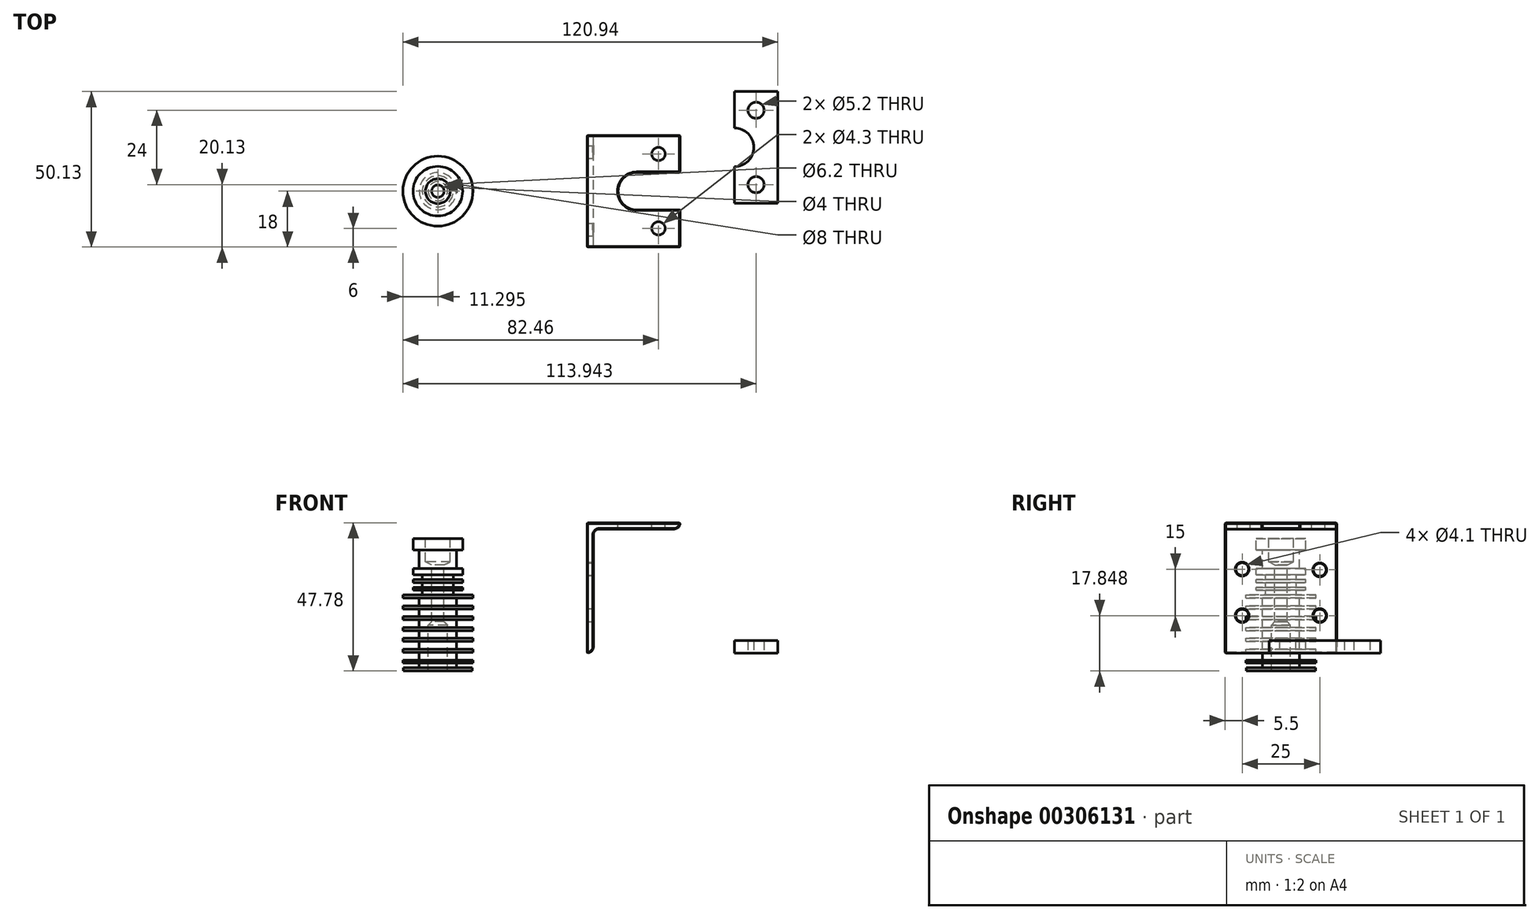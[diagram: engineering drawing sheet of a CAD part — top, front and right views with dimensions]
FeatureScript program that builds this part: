
annotation { "Feature Type Name" : "Feature", "Feature Type Description" : "" }
export const myFeature = defineFeature(function(context is Context, id is Id, definition is map)
    precondition{}
    {
        {
            var Q0;
            Q0=qCreatedBy(makeId("Front.planeOp"),FACE);
            var sketch = newSketch(context, id + "F0", { "sketchPlane" : qUnion([Q0])});
            skLineSegment(sketch, "E0", {"start": v(0, 0) * mm, "end": v(0, 42) * mm});
            skLineSegment(sketch, "E1", {"start": v(0, 42) * mm, "end": v(30, 42) * mm});
            skLineSegment(sketch, "E2", {"start": v(30, 42) * mm, "end": v(30, 40) * mm});
            skLineSegment(sketch, "E3", {"start": v(30, 40) * mm, "end": v(2, 40) * mm});
            skLineSegment(sketch, "E4", {"start": v(2, 40) * mm, "end": v(2, 0) * mm});
            skLineSegment(sketch, "E5", {"start": v(2, 0) * mm, "end": v(0, 0) * mm});
            skSolve(sketch);
        }
        {
            var Q0;
            Q0=makeQuery(id+"F0.imprint","IMPRINT",FACE,{"disambiguationData":[TD([[makeQuery(id+"F0.imprint","IMPRINT",EDGE,{"derivedFrom":sQuery(id+"F0.wireOp",EDGE,"E0")}),-1.0]])]});
            extrude(context, id + "F1", {"entities" : qUnion([Q0]), "endBound" : BoundingType.SYMMETRIC, "depth" : 36 * mm});
        }
        {
            var Q0;
            Q0=makeQuery(id+"F1.opExtrude","SWEPT_EDGE",EDGE,{"disambiguationData":[OSD([sQuery(id+"F0.wireOp",EDGE,"E3"),sQuery(id+"F0.wireOp",EDGE,"E4")])]});
            var Q1;
            Q1=makeQuery(id+"F1.opExtrude","SWEPT_EDGE",EDGE,{"disambiguationData":[OSD([sQuery(id+"F0.wireOp",EDGE,"E2"),sQuery(id+"F0.wireOp",EDGE,"E3")])]});
            var Q2;
            Q2=makeQuery(id+"F1.opExtrude","SWEPT_EDGE",EDGE,{"disambiguationData":[OSD([sQuery(id+"F0.wireOp",EDGE,"E4"),sQuery(id+"F0.wireOp",EDGE,"E5")])]});
            fillet(context, id + "F2", {"entities" : qUnion([Q0, Q1, Q2]), "radius" : 2 * mm, "tangentPropagation" : true, "allowEdgeOverflow" : false});
        }
        {
            var Q0;
            Q0=makeQuery(id+"F1.opExtrude","SWEPT_FACE",FACE,{"disambiguationData":[OSD([sQuery(id+"F0.wireOp",EDGE,"E1")])]});
            var sketch = newSketch(context, id + "F3", { "sketchPlane" : qUnion([Q0])});
            skArc(sketch, "E6", {"start": v(16, 6.03) * mm, "mid": v(9.97, 0) * mm, "end": v(16, -6.03) * mm});
            skLineSegment(sketch, "E7", {"start": v(16, -6.03) * mm, "end": v(30, -6.03) * mm});
            skLineSegment(sketch, "E8", {"start": v(16, 6.03) * mm, "end": v(30, 6.03) * mm});
            skLineSegment(sketch, "E9", {"start": v(30, -6.03) * mm, "end": v(30, 6.03) * mm});
            skCircle(sketch, "E10", {"center": v(23, 12) * mm, "radius": 2.15 * mm});
            skCircle(sketch, "E11", {"center": v(23, -12) * mm, "radius": 2.15 * mm});
            skSolve(sketch);
        }
        {
            var Q0;
            Q0=makeQuery(id+"F3.imprint","IMPRINT",FACE,{"disambiguationData":[TD([[makeQuery(id+"F3.imprint","IMPRINT",EDGE,{"derivedFrom":sQuery(id+"F3.wireOp",EDGE,"E6")}),1.0]])]});
            extrude(context, id + "F4", {"entities" : qUnion([Q0]), "operationType" : NewBodyOperationType.REMOVE, "oppositeDirection" : true, "depth" : 25 * mm});
        }
        {
            var Q0;
            Q0=makeQuery(id+"F1.opExtrude","SWEPT_FACE",FACE,{"disambiguationData":[OSD([sQuery(id+"F0.wireOp",EDGE,"E0")])]});
            var sketch = newSketch(context, id + "F5", { "sketchPlane" : qUnion([Q0])});
            skPoint(sketch, "E12", {"position": v(-12.5, 26.84) * mm});
            skPoint(sketch, "E13", {"position": v(-12.5, 12.07) * mm});
            skPoint(sketch, "E14", {"position": v(12.5, 12.07) * mm});
            skPoint(sketch, "E15", {"position": v(12.5, 27.07) * mm});
            skCircle(sketch, "E16", {"center": v(-12.5, 26.84) * mm, "radius": 2.05 * mm});
            skCircle(sketch, "E17", {"center": v(-12.5, 12.07) * mm, "radius": 2.05 * mm});
            skCircle(sketch, "E18", {"center": v(12.5, 12.07) * mm, "radius": 2.05 * mm});
            skCircle(sketch, "E19", {"center": v(12.5, 27.07) * mm, "radius": 2.05 * mm});
            skSolve(sketch);
        }
        {
            var Q0;
            Q0=makeQuery(id+"F5.imprint","IMPRINT",FACE,{"disambiguationData":[TD([[makeQuery(id+"F5.imprint","IMPRINT",EDGE,{"derivedFrom":sQuery(id+"F5.wireOp",EDGE,"E16")}),1.0]])]});
            var Q1;
            Q1=makeQuery(id+"F5.imprint","IMPRINT",FACE,{"disambiguationData":[TD([[makeQuery(id+"F5.imprint","IMPRINT",EDGE,{"derivedFrom":sQuery(id+"F5.wireOp",EDGE,"E17")}),1.0]])]});
            var Q2;
            Q2=makeQuery(id+"F5.imprint","IMPRINT",FACE,{"disambiguationData":[TD([[makeQuery(id+"F5.imprint","IMPRINT",EDGE,{"derivedFrom":sQuery(id+"F5.wireOp",EDGE,"E18")}),1.0]])]});
            var Q3;
            Q3=makeQuery(id+"F5.imprint","IMPRINT",FACE,{"disambiguationData":[TD([[makeQuery(id+"F5.imprint","IMPRINT",EDGE,{"derivedFrom":sQuery(id+"F5.wireOp",EDGE,"E19")}),1.0]])]});
            extrude(context, id + "F6", {"entities" : qUnion([Q0, Q1, Q2, Q3]), "operationType" : NewBodyOperationType.REMOVE, "oppositeDirection" : true, "depth" : 25 * mm});
        }
        {
            var Q0;
            Q0=makeQuery(id+"F1.opExtrude","SWEPT_FACE",FACE,{"disambiguationData":[OSD([sQuery(id+"F0.wireOp",EDGE,"E0")])]});
            var Q1;
            Q1=makeQuery(id+"F1.opExtrude","SWEPT_FACE",FACE,{"disambiguationData":[OSD([sQuery(id+"F0.wireOp",EDGE,"E1")])]});
            var Q2;
            Q2=makeQuery(id+"F1.opExtrude","SWEPT_FACE",FACE,{"disambiguationData":[OSD([sQuery(id+"F0.wireOp",EDGE,"E4")])]});
            var Q3;
            Q3=makeQuery(id+"F1.opExtrude","SWEPT_FACE",FACE,{"disambiguationData":[OSD([sQuery(id+"F0.wireOp",EDGE,"E3")])]});
            chamfer(context, id + "F7", {"entities" : qUnion([Q0, Q1, Q2, Q3]), "width" : 0.2 * mm, "tangentPropagation" : true});
        }
        {
            var Q0;
            Q0 = qSketchRegion(id + "F3", true);
            extrude(context, id + "F8", {"entities" : qUnion([Q0]), "operationType" : NewBodyOperationType.REMOVE, "oppositeDirection" : true, "depth" : 25 * mm});
        }
        {
            var Q0;
            Q0=qCreatedBy(makeId("Top.planeOp"),FACE);
            var sketch = newSketch(context, id + "F9", { "sketchPlane" : qUnion([Q0])});
            skLineSegment(sketch, "E20.bottom", {"start": v(47.48, -3.87) * mm, "end": v(61.48, -3.87) * mm});
            skLineSegment(sketch, "E20.top", {"start": v(47.48, 32.13) * mm, "end": v(61.48, 32.13) * mm});
            skLineSegment(sketch, "E20.left", {"start": v(47.48, -3.87) * mm, "end": v(47.48, 7.88) * mm});
            skLineSegment(sketch, "E20.right", {"start": v(61.48, -3.87) * mm, "end": v(61.48, 32.13) * mm});
            skArc(sketch, "E21", {"start": v(47.48, 7.88) * mm, "mid": v(53.73, 14.13) * mm, "end": v(47.48, 20.38) * mm});
            skLineSegment(sketch, "E22.trimOffspring", {"start": v(47.48, 20.38) * mm, "end": v(47.48, 32.13) * mm});
            skCircle(sketch, "E23", {"center": v(54.48, 26.13) * mm, "radius": 2.6 * mm});
            skPoint(sketch, "E23.centerSnap0", {"position": v(54.48, 32.13) * mm});
            skCircle(sketch, "E24", {"center": v(54.48, 2.13) * mm, "radius": 2.6 * mm});
            skSolve(sketch);
        }
        {
            var Q0;
            Q0=makeQuery(id+"F9.imprint","IMPRINT",FACE,{"disambiguationData":[TD([[makeQuery(id+"F9.imprint","IMPRINT",EDGE,{"derivedFrom":sQuery(id+"F9.wireOp",EDGE,"E20.bottom")}),1.0]])]});
            extrude(context, id + "F10", {"entities" : qUnion([Q0]), "depth" : 4 * mm});
        }
        {
            var Q0;
            Q0=qCreatedBy(makeId("Front.planeOp"),FACE);
            var sketch = newSketch(context, id + "F11", { "sketchPlane" : qUnion([Q0])});
            skLineSegment(sketch, "E25", {"start": v(-59.31, -5.78) * mm, "end": v(-51.26, -5.78) * mm});
            skLineSegment(sketch, "E26", {"start": v(-59.31, -5.78) * mm, "end": v(-59.31, -4.78) * mm});
            skLineSegment(sketch, "E27", {"start": v(-59.31, -4.78) * mm, "end": v(-54.16, -4.78) * mm});
            skPoint(sketch, "E28", {"position": v(-54.16, -4.78) * mm});
            skPoint(sketch, "E29", {"position": v(-54.16, -2.28) * mm});
            skPoint(sketch, "E30", {"position": v(-54.16, 1.22) * mm});
            skPoint(sketch, "E31", {"position": v(-54.16, 4.72) * mm});
            skPoint(sketch, "E32", {"position": v(-54.16, 8.22) * mm});
            skPoint(sketch, "E33", {"position": v(-54.16, 11.72) * mm});
            skPoint(sketch, "E34", {"position": v(-54.16, 15.22) * mm});
            skPoint(sketch, "E35", {"position": v(-59.46, -2.28) * mm});
            skPoint(sketch, "E36", {"position": v(-59.46, 1.22) * mm});
            skPoint(sketch, "E37", {"position": v(-59.46, 4.72) * mm});
            skPoint(sketch, "E38", {"position": v(-59.46, 8.22) * mm});
            skPoint(sketch, "E39", {"position": v(-59.46, 11.72) * mm});
            skPoint(sketch, "E40", {"position": v(-59.46, 15.22) * mm});
            skPoint(sketch, "E41", {"position": v(-59.46, 18.72) * mm});
            skLineSegment(sketch, "E42", {"start": v(-59.46, -3.28) * mm, "end": v(-54.16, -3.28) * mm});
            skLineSegment(sketch, "E43", {"start": v(-59.46, -3.28) * mm, "end": v(-59.46, -2.28) * mm});
            skLineSegment(sketch, "E44", {"start": v(-59.46, -2.28) * mm, "end": v(-54.16, -2.28) * mm});
            skLineSegment(sketch, "E45", {"start": v(-59.46, 0.22) * mm, "end": v(-54.16, 0.22) * mm});
            skLineSegment(sketch, "E46", {"start": v(-59.46, 0.22) * mm, "end": v(-59.46, 1.22) * mm});
            skLineSegment(sketch, "E47", {"start": v(-59.46, 1.22) * mm, "end": v(-54.16, 1.22) * mm});
            skLineSegment(sketch, "E48", {"start": v(-59.46, 3.72) * mm, "end": v(-54.16, 3.72) * mm});
            skLineSegment(sketch, "E49", {"start": v(-59.46, 3.72) * mm, "end": v(-59.46, 4.72) * mm});
            skLineSegment(sketch, "E50", {"start": v(-59.46, 4.72) * mm, "end": v(-54.16, 4.72) * mm});
            skLineSegment(sketch, "E51", {"start": v(-59.46, 7.22) * mm, "end": v(-54.16, 7.22) * mm});
            skLineSegment(sketch, "E52", {"start": v(-59.46, 7.22) * mm, "end": v(-59.46, 8.22) * mm});
            skLineSegment(sketch, "E53", {"start": v(-59.46, 10.72) * mm, "end": v(-54.16, 10.72) * mm});
            skLineSegment(sketch, "E54", {"start": v(-59.46, 10.72) * mm, "end": v(-59.46, 11.72) * mm});
            skLineSegment(sketch, "E55", {"start": v(-59.46, 11.72) * mm, "end": v(-54.16, 11.72) * mm});
            skLineSegment(sketch, "E56", {"start": v(-59.46, 14.22) * mm, "end": v(-54.16, 14.22) * mm});
            skLineSegment(sketch, "E57", {"start": v(-59.46, 14.22) * mm, "end": v(-59.46, 15.22) * mm});
            skLineSegment(sketch, "E58", {"start": v(-59.46, 15.22) * mm, "end": v(-54.16, 15.22) * mm});
            skLineSegment(sketch, "E59", {"start": v(-59.46, 17.72) * mm, "end": v(-54.16, 17.72) * mm});
            skLineSegment(sketch, "E60", {"start": v(-59.46, 17.72) * mm, "end": v(-59.46, 18.72) * mm});
            skLineSegment(sketch, "E61", {"start": v(-54.16, -4.78) * mm, "end": v(-54.16, -3.28) * mm});
            skLineSegment(sketch, "E62", {"start": v(-54.16, -2.28) * mm, "end": v(-54.16, 0.22) * mm});
            skLineSegment(sketch, "E63", {"start": v(-54.16, 1.22) * mm, "end": v(-54.16, 3.72) * mm});
            skLineSegment(sketch, "E64", {"start": v(-54.16, 4.72) * mm, "end": v(-54.16, 7.22) * mm});
            skLineSegment(sketch, "E65", {"start": v(-54.16, 8.22) * mm, "end": v(-54.16, 10.72) * mm});
            skLineSegment(sketch, "E66", {"start": v(-54.16, 11.72) * mm, "end": v(-54.16, 14.22) * mm});
            skLineSegment(sketch, "E67", {"start": v(-54.16, 15.22) * mm, "end": v(-54.16, 17.72) * mm});
            skPoint(sketch, "E68", {"position": v(-48.16, -5.78) * mm});
            skLineSegment(sketch, "E69", {"start": v(-59.46, 8.22) * mm, "end": v(-54.16, 8.22) * mm});
            skLineSegment(sketch, "E70", {"start": v(-56.16, 27.22) * mm, "end": v(-54.16, 27.22) * mm});
            skLineSegment(sketch, "E71", {"start": v(-54.16, 27.22) * mm, "end": v(-54.16, 33.22) * mm});
            skLineSegment(sketch, "E72", {"start": v(-54.16, 33.22) * mm, "end": v(-56.16, 33.22) * mm});
            skLineSegment(sketch, "E73", {"start": v(-56.16, 33.22) * mm, "end": v(-56.16, 36.92) * mm});
            skLineSegment(sketch, "E74", {"start": v(-56.16, 36.92) * mm, "end": v(-52.16, 36.92) * mm});
            skLineSegment(sketch, "E75", {"start": v(-59.46, 18.72) * mm, "end": v(-53.16, 18.72) * mm});
            skLineSegment(sketch, "E76", {"start": v(-53.16, 18.72) * mm, "end": v(-53.16, 20.22) * mm});
            skLineSegment(sketch, "E77", {"start": v(-53.16, 20.22) * mm, "end": v(-56.16, 20.22) * mm});
            skPoint(sketch, "E78", {"position": v(-52.16, 36.92) * mm});
            skLineSegment(sketch, "E79", {"start": v(-52.16, 36.92) * mm, "end": v(-52.16, 29.42) * mm});
            skPoint(sketch, "E80", {"position": v(-50.16, 28.42) * mm});
            skLineSegment(sketch, "E81", {"start": v(-52.16, 29.42) * mm, "end": v(-50.16, 28.42) * mm});
            skLineSegment(sketch, "E82", {"start": v(-50.16, 28.42) * mm, "end": v(-50.16, 10.14) * mm});
            skPoint(sketch, "E83", {"position": v(-51.26, -5.78) * mm});
            skLineSegment(sketch, "E84", {"start": v(-51.26, -5.78) * mm, "end": v(-51.26, 9.02) * mm});
            skLineSegment(sketch, "E85", {"start": v(-51.26, 9.02) * mm, "end": v(-50.16, 10.14) * mm});
            skLineSegment(sketch, "E86", {"start": v(-56.16, 20.22) * mm, "end": v(-56.16, 21.22) * mm});
            skLineSegment(sketch, "E87", {"start": v(-56.16, 21.22) * mm, "end": v(-53.16, 21.22) * mm});
            skLineSegment(sketch, "E88", {"start": v(-53.16, 21.22) * mm, "end": v(-53.16, 22.72) * mm});
            skLineSegment(sketch, "E89", {"start": v(-53.16, 22.72) * mm, "end": v(-56.16, 22.72) * mm});
            skLineSegment(sketch, "E90", {"start": v(-56.16, 22.72) * mm, "end": v(-56.16, 23.72) * mm});
            skLineSegment(sketch, "E91", {"start": v(-56.16, 23.72) * mm, "end": v(-53.16, 23.72) * mm});
            skLineSegment(sketch, "E92", {"start": v(-53.16, 23.72) * mm, "end": v(-53.16, 25.22) * mm});
            skLineSegment(sketch, "E93", {"start": v(-53.16, 25.22) * mm, "end": v(-56.16, 25.22) * mm});
            skLineSegment(sketch, "E94", {"start": v(-56.16, 25.22) * mm, "end": v(-56.16, 27.22) * mm});
            skLineSegment(sketch, "E95", {"start": v(-48.16, 41.06) * mm, "end": v(-48.16, -5.78) * mm});
            skSolve(sketch);
        }
        {
            var Q0;
            Q0=makeQuery(id+"F11.imprint","IMPRINT",FACE,{"disambiguationData":[TD([[makeQuery(id+"F11.imprint","IMPRINT",EDGE,{"derivedFrom":sQuery(id+"F11.wireOp",EDGE,"E25")}),1.0]])]});
            var Q1;
            Q1=sQuery(id+"F11.wireOp",EDGE,"E95");
            revolve(context, id + "F12", {"entities" : qUnion([Q0]), "axis" : qUnion([Q1]), "revolveType" : RevolveType.FULL});
        }
    });
